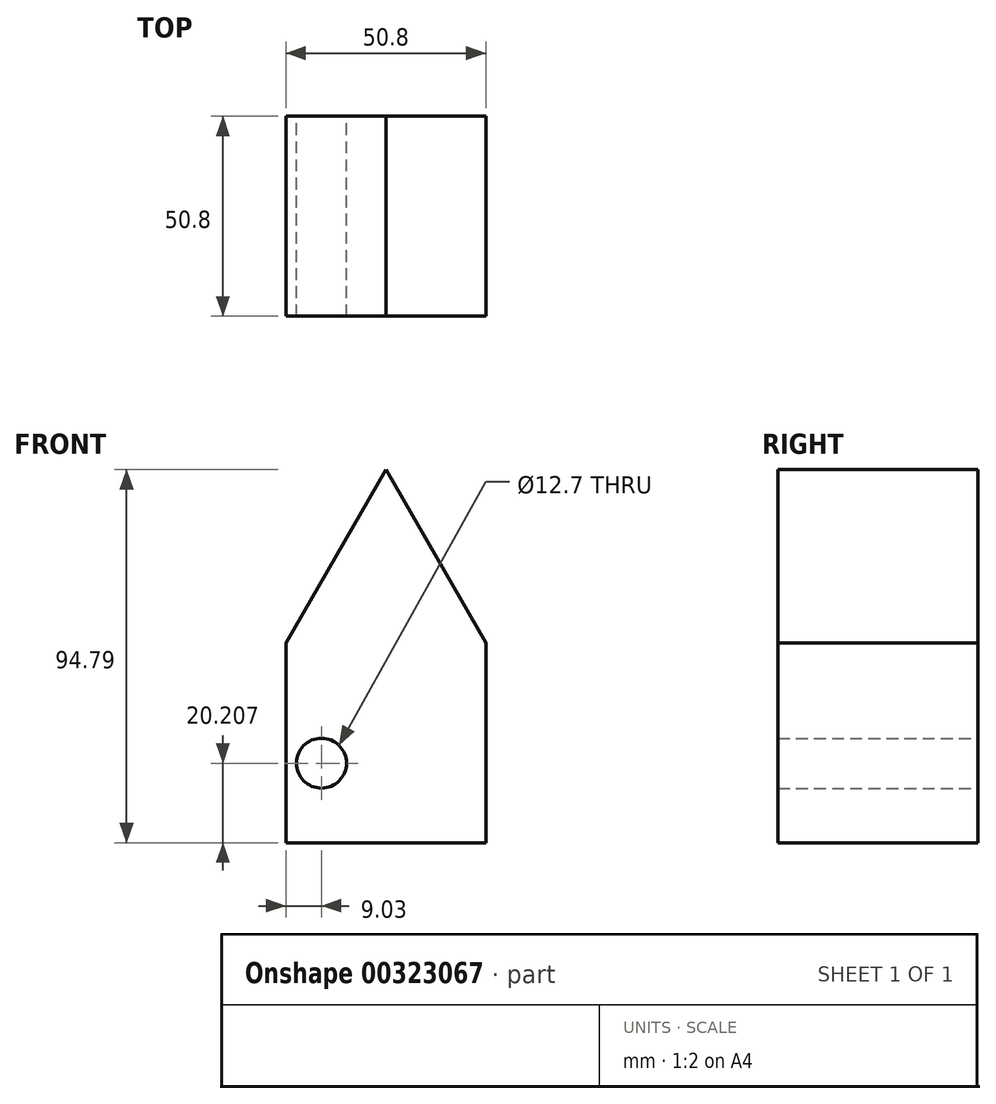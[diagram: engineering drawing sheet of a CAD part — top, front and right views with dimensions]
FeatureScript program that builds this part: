
annotation { "Feature Type Name" : "Feature", "Feature Type Description" : "" }
export const myFeature = defineFeature(function(context is Context, id is Id, definition is map)
    precondition{}
    {
        {
            var Q0;
            Q0=qCreatedBy(makeId("Front.planeOp"),FACE);
            var sketch = newSketch(context, id + "F0", { "sketchPlane" : qUnion([Q0])});
            skLineSegment(sketch, "E0.top", {"start": v(-17.62, -37.33) * mm, "end": v(33.18, -37.33) * mm});
            skLineSegment(sketch, "E0.left", {"start": v(-17.62, 13.47) * mm, "end": v(-17.62, -37.33) * mm});
            skLineSegment(sketch, "E0.right", {"start": v(33.18, 13.47) * mm, "end": v(33.18, -37.33) * mm});
            skLineSegment(sketch, "E1", {"start": v(-17.62, 13.47) * mm, "end": v(7.78, 57.46) * mm});
            skLineSegment(sketch, "E2", {"start": v(7.78, 57.46) * mm, "end": v(33.18, 13.47) * mm});
            skCircle(sketch, "E3", {"center": v(-8.59, -17.12) * mm, "radius": 6.35 * mm});
            skSolve(sketch);
        }
        {
            var Q0;
            Q0=makeQuery(id+"F0.imprint","IMPRINT",FACE,{"disambiguationData":[TD([[makeQuery(id+"F0.imprint","IMPRINT",EDGE,{"derivedFrom":sQuery(id+"F0.wireOp",EDGE,"E0.top")}),1.0]])]});
            extrude(context, id + "F1", {"entities" : qUnion([Q0]), "depth" : 50.8 * mm});
        }
    });
